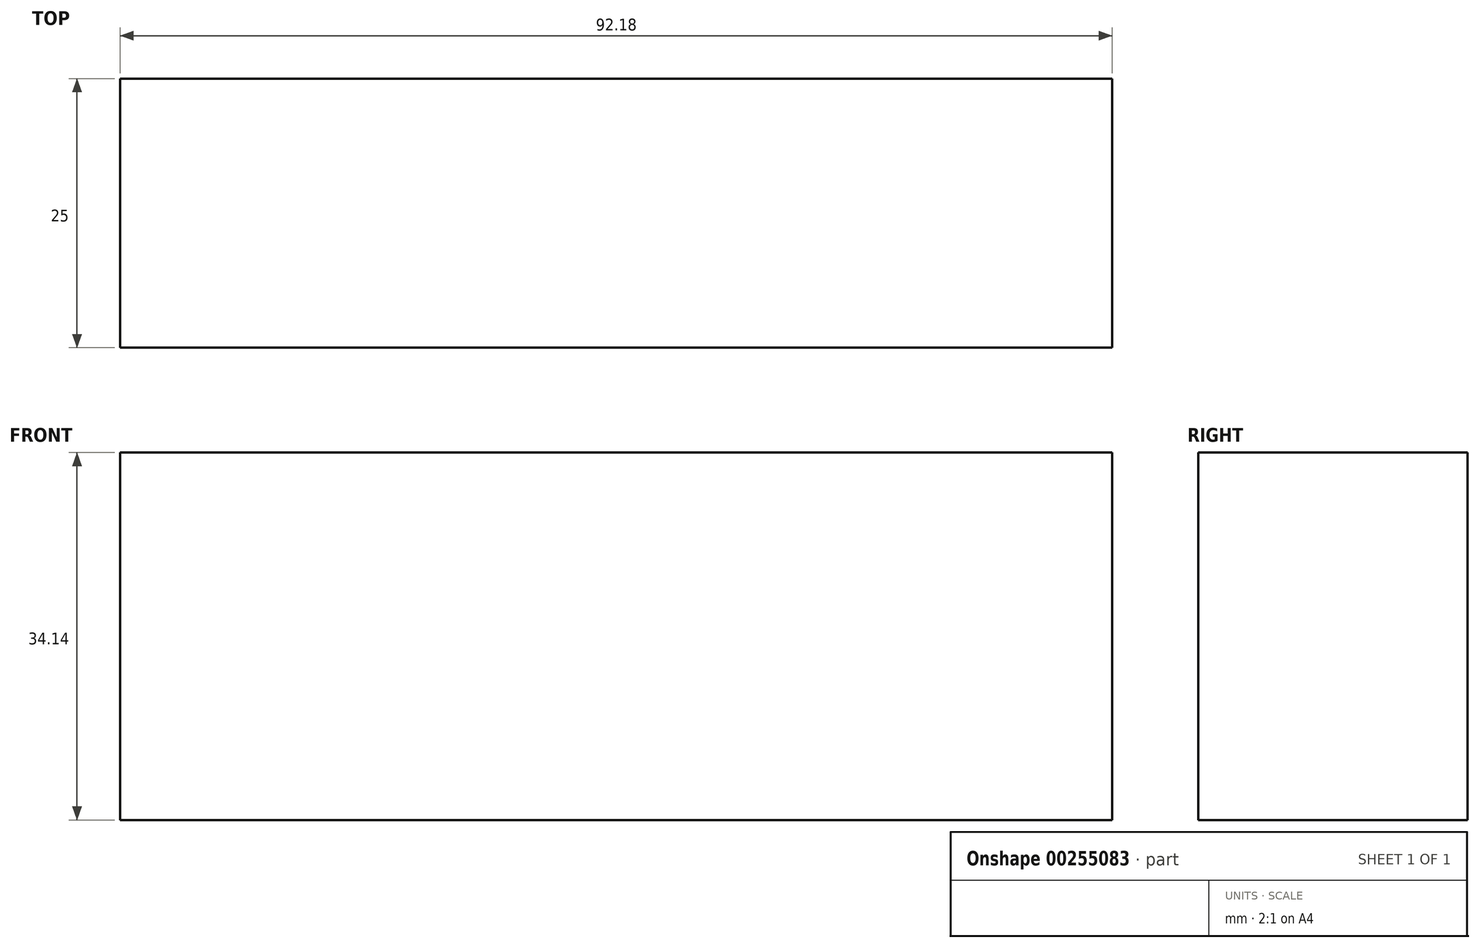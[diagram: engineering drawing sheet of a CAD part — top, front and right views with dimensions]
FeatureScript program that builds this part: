
annotation { "Feature Type Name" : "Feature", "Feature Type Description" : "" }
export const myFeature = defineFeature(function(context is Context, id is Id, definition is map)
    precondition{}
    {
        {
            var Q0;
            Q0=qCreatedBy(makeId("Front.planeOp"),FACE);
            var sketch = newSketch(context, id + "F0", { "sketchPlane" : qUnion([Q0])});
            skLineSegment(sketch, "E0.bottom", {"start": v(46.1, -17.07) * mm, "end": v(-46.1, -17.07) * mm});
            skLineSegment(sketch, "E0.top", {"start": v(46.1, 17.07) * mm, "end": v(-46.1, 17.07) * mm});
            skLineSegment(sketch, "E0.left", {"start": v(46.1, -17.07) * mm, "end": v(46.1, 17.07) * mm});
            skLineSegment(sketch, "E0.right", {"start": v(-46.1, -17.07) * mm, "end": v(-46.1, 17.07) * mm});
            skPoint(sketch, "E0.middle", {"position": v(0, 0) * mm});
            skSolve(sketch);
        }
        {
            var Q0;
            Q0=makeQuery(id+"F0.imprint","IMPRINT",FACE,{"disambiguationData":[TD([[makeQuery(id+"F0.imprint","IMPRINT",EDGE,{"derivedFrom":sQuery(id+"F0.wireOp",EDGE,"E0.bottom")}),-1.0]])]});
            extrude(context, id + "F1", {"entities" : qUnion([Q0]), "depth" : 25 * mm});
        }
    });
